# Revit family: Deckel für T-Abzweigstück Magic, Bei NB 100-200
name_source: partatom
category: Generic Models
revit_build: Autodesk Revit 2015 (Build: 20140606_1530(x64)
units: mm (PartAtom-declared; Revit-internal decimal feet)

## types (6) — shared parameters
Height = 1 mm  [stored 0.00328084 ft]
Height 1 = 2 mm  [stored 0.00656168 ft]
Length 1 = 5 mm  [stored 0.0164042 ft]
Manufacturer = OBO Bettermann
URL = http://www.obo-bettermann.com

## per-type parameters (varying)
| type | GTIN | Length | Length 2 | Manufacturer Art.No. | Material | Width | Width 1 |
| DFTM 100 FS | 4012195930884 | 151 mm | 104 mm | 7138790 | Strip-galvanised | 197 mm | 99 mm |
| DFTM 150 FS | 4012195930891 | 201 mm | 154 mm  [stored 0.505249 ft] | 7138792 | Strip-galvanised | 247 mm | 124 mm |
| DFTM 200 FS | 4012195930907 | 251 mm | 204 mm | 7138794 | Strip-galvanised | 297 mm | 149 mm |
| DFTM 100 DD | 4012195930952 | 151 mm | 104 mm | 7138830 | Strip galvanised zinc/aluminium, Double Dip | 197 mm | 99 mm |
| DFTM 150 DD | 4012195930969 | 201 mm | 154 mm  [stored 0.505249 ft] | 7138832 | Strip galvanised zinc/aluminium, Double Dip | 247 mm | 124 mm |
| DFTM 200 DD | 4012195931003 | 251 mm | 204 mm | 7138834 | Strip galvanised zinc/aluminium, Double Dip | 297 mm | 149 mm |

note: column(s) folded — value = type name in every type: Article Type

note: [stored X ft] marks values corroborated as IEEE doubles in the binary element streams (Revit-internal decimal feet)

## geometry (parser evidence)
native form markers: Sweep x1
no freeform markers — native parametric forms only
